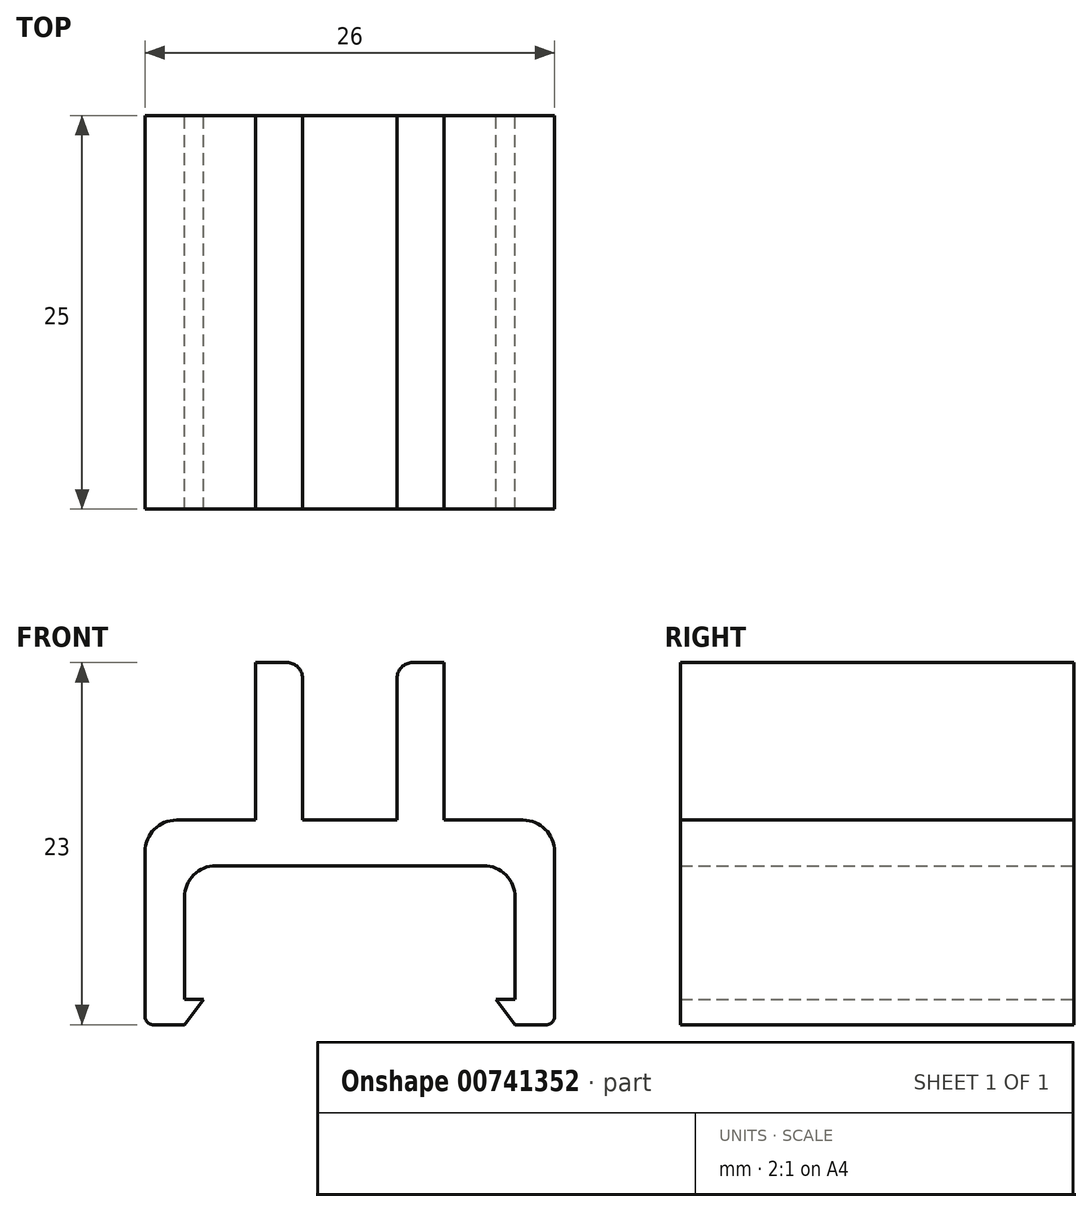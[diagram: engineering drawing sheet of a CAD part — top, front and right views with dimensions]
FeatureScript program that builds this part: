
annotation { "Feature Type Name" : "Feature", "Feature Type Description" : "" }
export const myFeature = defineFeature(function(context is Context, id is Id, definition is map)
    precondition{}
    {
        {
            var Q0;
            Q0=qCreatedBy(makeId("Front.planeOp"),FACE);
            var sketch = newSketch(context, id + "F0", { "sketchPlane" : qUnion([Q0])});
            skLineSegment(sketch, "E0", {"start": v(-13.5, -6.98) * mm, "end": v(7.5, -6.98) * mm});
            skLineSegment(sketch, "E1", {"start": v(7.5, -6.98) * mm, "end": v(7.5, -15.48) * mm});
            skLineSegment(sketch, "E2", {"start": v(-13.5, -6.98) * mm, "end": v(-13.5, -15.48) * mm});
            skLineSegment(sketch, "E3", {"start": v(7.5, -15.48) * mm, "end": v(6.3, -15.48) * mm});
            skLineSegment(sketch, "E4", {"start": v(6.3, -15.48) * mm, "end": v(7.5, -17.08) * mm});
            skLineSegment(sketch, "E5", {"start": v(7.5, -17.08) * mm, "end": v(10, -17.08) * mm});
            skLineSegment(sketch, "E6", {"start": v(10, -17.08) * mm, "end": v(10, -4.08) * mm});
            skLineSegment(sketch, "E7", {"start": v(10, -4.08) * mm, "end": v(3, -4.08) * mm});
            skLineSegment(sketch, "E8", {"start": v(3, -4.08) * mm, "end": v(3, 5.92) * mm});
            skLineSegment(sketch, "E9", {"start": v(3, 5.92) * mm, "end": v(0, 5.92) * mm});
            skLineSegment(sketch, "E10", {"start": v(0, 5.92) * mm, "end": v(0, -4.08) * mm});
            skLineSegment(sketch, "E11", {"start": v(0, -4.08) * mm, "end": v(-6, -4.08) * mm});
            skLineSegment(sketch, "E12", {"start": v(-6, -4.08) * mm, "end": v(-6, 5.92) * mm});
            skLineSegment(sketch, "E13", {"start": v(-6, 5.92) * mm, "end": v(-9, 5.92) * mm});
            skLineSegment(sketch, "E14", {"start": v(-9, 5.92) * mm, "end": v(-9, -4.08) * mm});
            skLineSegment(sketch, "E15", {"start": v(-9, -4.08) * mm, "end": v(-16, -4.08) * mm});
            skLineSegment(sketch, "E16", {"start": v(-16, -4.08) * mm, "end": v(-16, -17.08) * mm});
            skLineSegment(sketch, "E17", {"start": v(-16, -17.08) * mm, "end": v(-13.5, -17.08) * mm});
            skLineSegment(sketch, "E18", {"start": v(-13.5, -15.48) * mm, "end": v(-12.3, -15.48) * mm});
            skLineSegment(sketch, "E19", {"start": v(-13.5, -17.08) * mm, "end": v(-12.3, -15.48) * mm});
            skSolve(sketch);
        }
        {
            var Q0;
            Q0=makeQuery(id+"F0.imprint","IMPRINT",FACE,{"disambiguationData":[TD([[makeQuery(id+"F0.imprint","IMPRINT",EDGE,{"derivedFrom":sQuery(id+"F0.wireOp",EDGE,"E0")}),1.0]])]});
            extrude(context, id + "F1", {"entities" : qUnion([Q0]), "depth" : 25 * mm, "offsetDistance" : 25 * mm});
        }
        {
            var Q0;
            Q0=makeQuery(id+"F1.opExtrude","SWEPT_EDGE",EDGE,{"disambiguationData":[OSD([sQuery(id+"F0.wireOp",EDGE,"E0"),sQuery(id+"F0.wireOp",EDGE,"E2")])]});
            var Q1;
            Q1=makeQuery(id+"F1.opExtrude","SWEPT_EDGE",EDGE,{"disambiguationData":[OSD([sQuery(id+"F0.wireOp",EDGE,"E0"),sQuery(id+"F0.wireOp",EDGE,"E1")])]});
            fillet(context, id + "F2", {"entities" : qUnion([Q0, Q1]), "radius" : 2 * mm, "tangentPropagation" : true, "allowEdgeOverflow" : false});
        }
        {
            var Q0;
            Q0=makeQuery(id+"F1.opExtrude","SWEPT_EDGE",EDGE,{"disambiguationData":[OSD([sQuery(id+"F0.wireOp",EDGE,"E6"),sQuery(id+"F0.wireOp",EDGE,"E7")])]});
            var Q1;
            Q1=makeQuery(id+"F1.opExtrude","SWEPT_EDGE",EDGE,{"disambiguationData":[OSD([sQuery(id+"F0.wireOp",EDGE,"E15"),sQuery(id+"F0.wireOp",EDGE,"E16")])]});
            fillet(context, id + "F3", {"entities" : qUnion([Q0, Q1]), "radius" : 2 * mm, "tangentPropagation" : true, "allowEdgeOverflow" : false});
        }
        {
            var Q0;
            Q0=makeQuery(id+"F1.opExtrude","SWEPT_EDGE",EDGE,{"disambiguationData":[OSD([sQuery(id+"F0.wireOp",EDGE,"E12"),sQuery(id+"F0.wireOp",EDGE,"E13")])]});
            var Q1;
            Q1=makeQuery(id+"F1.opExtrude","SWEPT_EDGE",EDGE,{"disambiguationData":[OSD([sQuery(id+"F0.wireOp",EDGE,"E9"),sQuery(id+"F0.wireOp",EDGE,"E10")])]});
            fillet(context, id + "F4", {"entities" : qUnion([Q0, Q1]), "radius" : 1 * mm, "tangentPropagation" : true, "allowEdgeOverflow" : false});
        }
        {
            var Q0;
            Q0=makeQuery(id+"F1.opExtrude","SWEPT_EDGE",EDGE,{"disambiguationData":[OSD([sQuery(id+"F0.wireOp",EDGE,"E5"),sQuery(id+"F0.wireOp",EDGE,"E6")])]});
            var Q1;
            Q1=makeQuery(id+"F1.opExtrude","SWEPT_EDGE",EDGE,{"disambiguationData":[OSD([sQuery(id+"F0.wireOp",EDGE,"E16"),sQuery(id+"F0.wireOp",EDGE,"E17")])]});
            fillet(context, id + "F5", {"entities" : qUnion([Q0, Q1]), "radius" : 0.5 * mm, "tangentPropagation" : true, "allowEdgeOverflow" : false});
        }
    });
